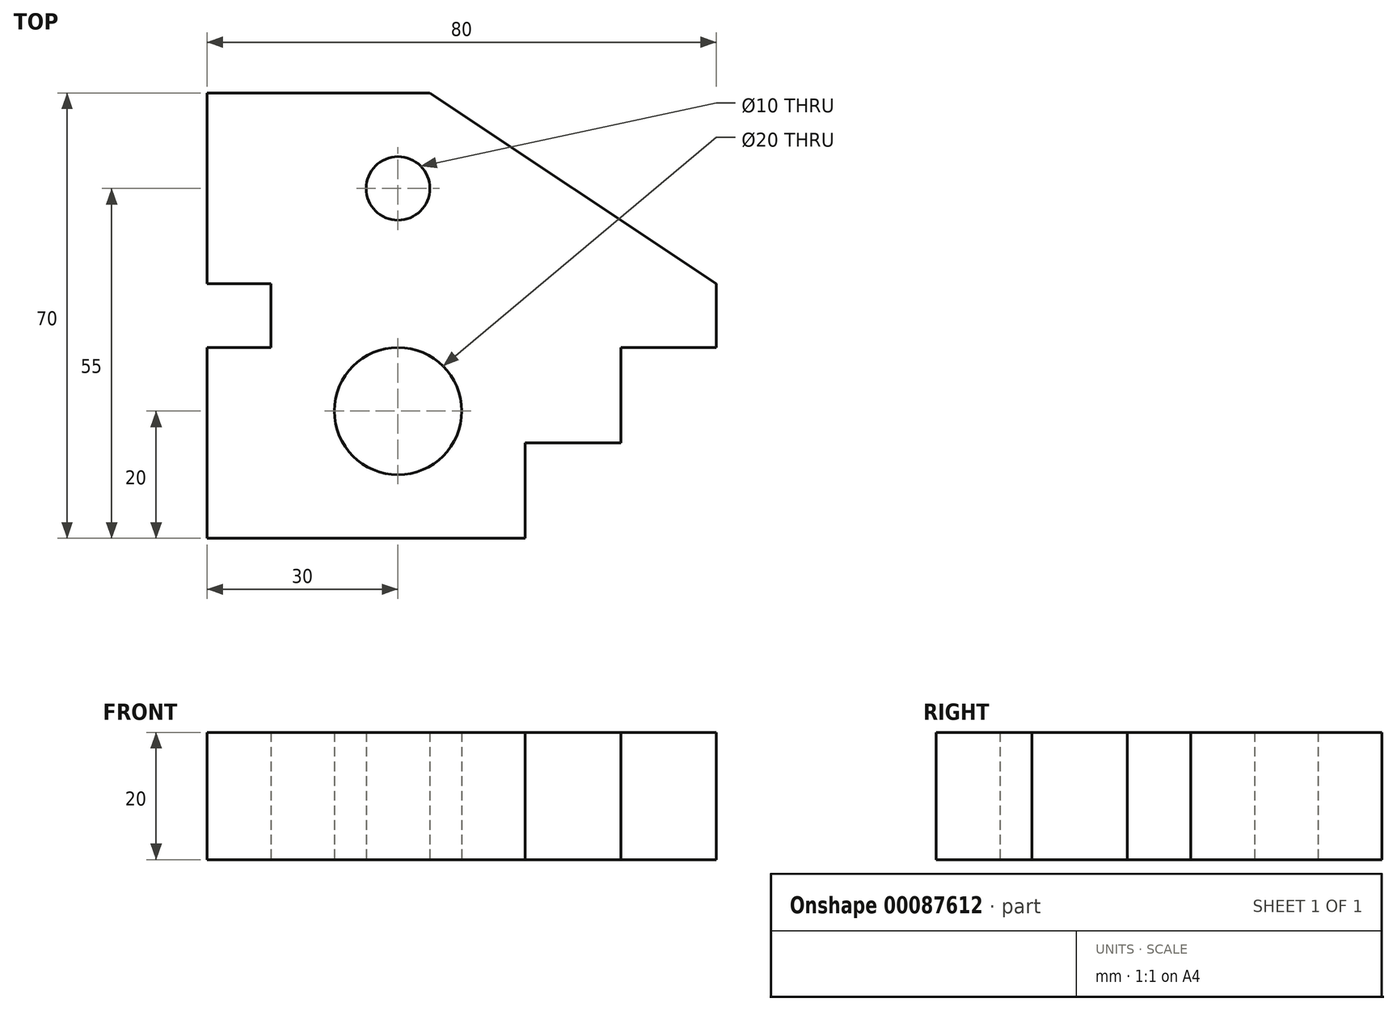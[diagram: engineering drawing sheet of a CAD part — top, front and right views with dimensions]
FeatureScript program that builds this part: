
annotation { "Feature Type Name" : "Feature", "Feature Type Description" : "" }
export const myFeature = defineFeature(function(context is Context, id is Id, definition is map)
    precondition{}
    {
        {
            var Q0;
            Q0=qCreatedBy(makeId("Top.planeOp"),FACE);
            var sketch = newSketch(context, id + "F0", { "sketchPlane" : qUnion([Q0])});
            skLineSegment(sketch, "E0", {"start": v(0, 0) * mm, "end": v(50, 0) * mm});
            skLineSegment(sketch, "E1", {"start": v(50, 0) * mm, "end": v(50, 15) * mm});
            skLineSegment(sketch, "E2", {"start": v(50, 15) * mm, "end": v(65, 15) * mm});
            skLineSegment(sketch, "E3", {"start": v(65, 15) * mm, "end": v(65, 30) * mm});
            skLineSegment(sketch, "E4", {"start": v(65, 30) * mm, "end": v(80, 30) * mm});
            skLineSegment(sketch, "E5", {"start": v(80, 30) * mm, "end": v(80, 40) * mm});
            skLineSegment(sketch, "E6", {"start": v(80, 40) * mm, "end": v(35, 70) * mm});
            skLineSegment(sketch, "E7", {"start": v(35, 70) * mm, "end": v(0, 70) * mm});
            skLineSegment(sketch, "E8", {"start": v(0, 70) * mm, "end": v(0, 40) * mm});
            skLineSegment(sketch, "E9", {"start": v(0, 40) * mm, "end": v(10, 40) * mm});
            skLineSegment(sketch, "E10", {"start": v(10, 40) * mm, "end": v(10, 30) * mm});
            skLineSegment(sketch, "E11", {"start": v(10, 30) * mm, "end": v(0, 30) * mm});
            skLineSegment(sketch, "E12", {"start": v(0, 30) * mm, "end": v(0, 0) * mm});
            skLineSegment(sketch, "E13", {"start": v(30, 20) * mm, "end": v(30, 55) * mm, "construction": true});
            skCircle(sketch, "E14", {"center": v(30, 55) * mm, "radius": 5 * mm});
            skCircle(sketch, "E15", {"center": v(30, 20) * mm, "radius": 10 * mm});
            skSolve(sketch);
        }
        {
            var Q0;
            Q0 = qSketchRegion(id + "F0", true);
            extrude(context, id + "F1", {"entities" : qUnion([Q0]), "depth" : 20 * mm});
        }
    });
